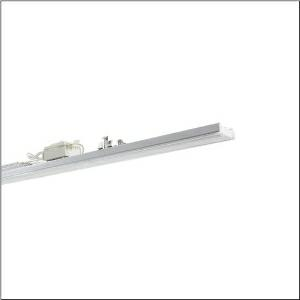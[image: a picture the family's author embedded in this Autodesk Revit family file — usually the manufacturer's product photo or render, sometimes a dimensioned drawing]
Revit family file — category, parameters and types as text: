
# Revit family: licross_21_recessed_ho_52tl18mn4e5m
name_source: partatom
category: Lighting Fixtures
units: mm (PartAtom-declared; Revit-internal decimal feet)

## family parameters
Cut with Voids When Loaded = No
Host = Face
Light Source = No
Part Type = Normal
Room Calculation Point = No
Round Connector Dimension = Use Diameter
Shared = No

## types (1)
- --- (1 x LED, 14940 lm, 83.1 W, 4000K)
    Apparent Load = 83 VA
    CIE Flux Codes = 75 94 99 100 100
    Color Rendering = 80
    Color Temperature = 4000K
    Default Elevation = 1800 mm
    Description = Licross 21 Recessed HO, luminaire insert, of sheet steel, galvanised, coil coated, white, length: 1.500mm, width: 66mm, height: 67mm, LED rated luminous flux: 14.940lm, light colour: 840, SDCM (Standard Deviation of Colour Matching)MacAdam ≤ 3 SDCM (initial), control gear: ON/OFF Multilumen, with plug, 3-pole, with phase selection, mains connection: 220..240V, AC, 50/60Hz, rated input power: 83W, internal wiring halogen-free, primary light control with lens, of plastic, primary optical cover: cover, of PMMA, light emission: direct distribution, primary light characteristic: symmetric, protection rating (complete): IP40, insulation class (complete): insulation class I (protective earthing), certification: CE, ENEC, VDE, UKCA, protection symbol: D if used in an environment without relevant dust loads with corresponding accessories, impact resistance: IK06, permissible ambient temperature for indoor applications: -35..+30°C, corresponds to IFS (International Featured Standards) requirements for safety and quality in the food industry, reducing of maximum allowable ambient temperature of 5°C with ceiling mounting, LABS conformity tested according to VDMA 24364:2018-05, The light source and the operating device comply with the requirements of the Ecodesign Regulation (EU) 2019/2020 and are replaceable in accordance with this regulation, packaging unit: 1 piece
    Height = 58 mm
    Lamp = 1 x LED
    Lamp Light Flux = 14940 lm
    Lamp Power = 83.1 W
    Lamp count = 1
    Length = 1500 mm
    Luminous efficacy = 180 lm/W
    Manufacturer = Siteco
    ModVariant = No
    Model = 52TL18MN4E5M
    Mounting Place = Ceiling
    Mounting Type = Pendant
    Number of Poles = 1
    OnlyDefault = Yes
    Power Factor = 1
    Product Name = Licross 21 Recessed HO
    Product group = luminaire insert | ceiling pendant
    ProductGroupID = 901
    Protection Class = Protection class I
    Protection Degree = IP 40
    RLX_Detail_Level = 1
    RLX_Emergency_Light_Flux = 0 lm
    RLX_Emergency_Type = 0
    RLX_Emergency_Type_DB = No
    RlxData = <blob elided: 22537 chars, md5=2ea10ad6>
    Socket = socket
    Standby Power = 0 W
    System Light Flux = 14940 lm
    System Power = 83 W
    Type Comments = factory setting: luminous flux: 100 % | (A | C | E) | 195 mA
    Type Image = l_1296930.jpg
    URL = http://relux.com
    VarID = @adj_107931
    Voltage = 0 V
    Weight = 0.00 kg
    Width = 66 mm

## geometry (parser evidence)
native form markers: Blend x4, Sweep x10
no freeform markers — native parametric forms only
